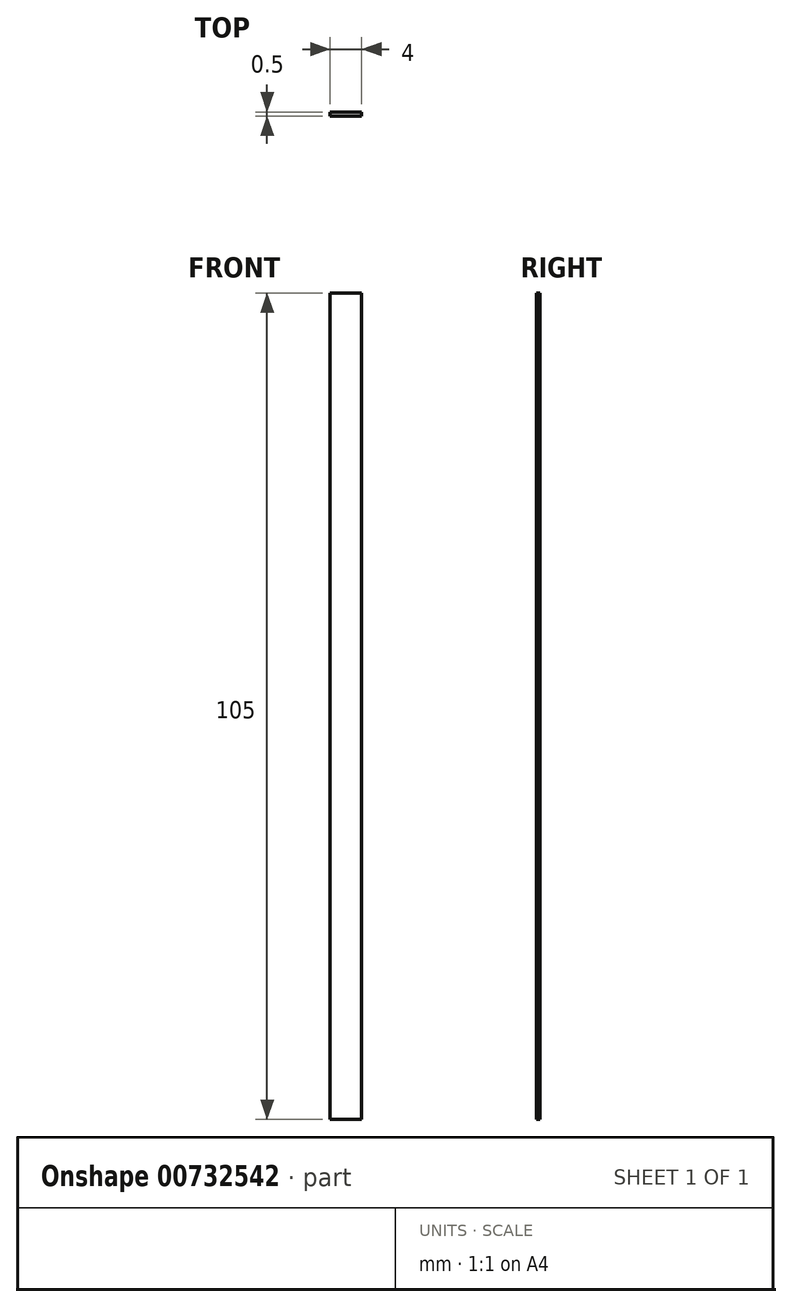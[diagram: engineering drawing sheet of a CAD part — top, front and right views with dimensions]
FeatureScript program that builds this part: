
annotation { "Feature Type Name" : "Feature", "Feature Type Description" : "" }
export const myFeature = defineFeature(function(context is Context, id is Id, definition is map)
    precondition{}
    {
        {
            var Q0;
            Q0=qCreatedBy(makeId("Top.planeOp"),FACE);
            var sketch = newSketch(context, id + "F0", { "sketchPlane" : qUnion([Q0])});
            skLineSegment(sketch, "E0.bottom", {"start": v(-4, 2.48) * mm, "end": v(0, 2.48) * mm});
            skLineSegment(sketch, "E0.top", {"start": v(-4, 1.98) * mm, "end": v(0, 1.98) * mm});
            skLineSegment(sketch, "E0.left", {"start": v(-4, 2.48) * mm, "end": v(-4, 1.98) * mm});
            skLineSegment(sketch, "E0.right", {"start": v(0, 2.48) * mm, "end": v(0, 1.98) * mm});
            skSolve(sketch);
        }
        {
            var Q0;
            Q0 = qSketchRegion(id + "F0", true);
            extrude(context, id + "F1", {"entities" : qUnion([Q0]), "depth" : 105 * mm, "offsetDistance" : 25 * mm});
        }
    });
